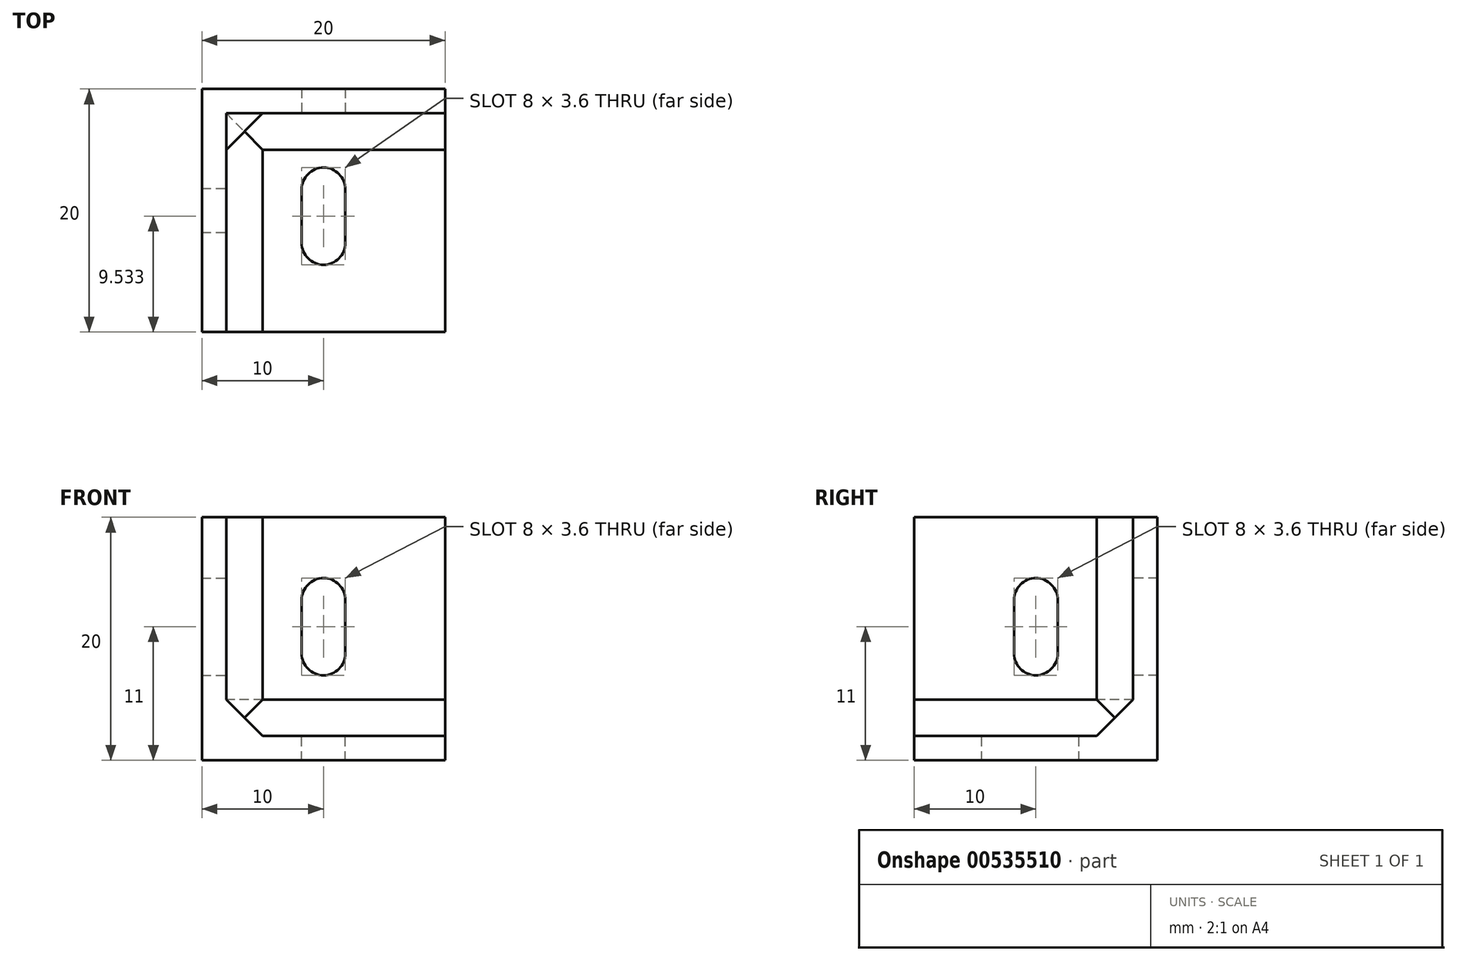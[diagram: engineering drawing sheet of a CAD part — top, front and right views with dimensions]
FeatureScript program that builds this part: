
annotation { "Feature Type Name" : "Feature", "Feature Type Description" : "" }
export const myFeature = defineFeature(function(context is Context, id is Id, definition is map)
    precondition{}
    {
        {
            var Q0;
            Q0=qCreatedBy(makeId("Top.planeOp"),FACE);
            var sketch = newSketch(context, id + "F0", { "sketchPlane" : qUnion([Q0])});
            skLineSegment(sketch, "E0.bottom", {"start": v(10, -10) * mm, "end": v(-10, -10) * mm});
            skLineSegment(sketch, "E0.top", {"start": v(10, 10) * mm, "end": v(-10, 10) * mm});
            skLineSegment(sketch, "E0.left", {"start": v(10, -10) * mm, "end": v(10, 10) * mm});
            skLineSegment(sketch, "E0.right", {"start": v(-10, -10) * mm, "end": v(-10, 10) * mm});
            skPoint(sketch, "E0.middle", {"position": v(0, 0) * mm});
            skSolve(sketch);
        }
        {
            var Q0;
            Q0=makeQuery(id+"F0.imprint","IMPRINT",FACE,{"disambiguationData":[TD([[makeQuery(id+"F0.imprint","IMPRINT",EDGE,{"derivedFrom":sQuery(id+"F0.wireOp",EDGE,"E0.bottom")}),-1.0]])]});
            extrude(context, id + "F1", {"entities" : qUnion([Q0]), "depth" : 2 * mm, "offsetDistance" : 25 * mm});
        }
        {
            var Q0;
            Q0=makeQuery(id+"F1.opExtrude","CAP_FACE",FACE,{"disambiguationData":[OSD([sQuery(id+"F0.wireOp",EDGE,"E0.bottom"),sQuery(id+"F0.wireOp",EDGE,"E0.top"),sQuery(id+"F0.wireOp",EDGE,"E0.left"),sQuery(id+"F0.wireOp",EDGE,"E0.right")])],"isStart":false});
            var sketch = newSketch(context, id + "F2", { "sketchPlane" : qUnion([Q0])});
            skLineSegment(sketch, "E1", {"start": v(-8, -10) * mm, "end": v(-10, -10) * mm});
            skLineSegment(sketch, "E2", {"start": v(-10, -10) * mm, "end": v(-10, 10) * mm});
            skLineSegment(sketch, "E3", {"start": v(-10, 10) * mm, "end": v(10, 10) * mm});
            skLineSegment(sketch, "E4", {"start": v(10, 10) * mm, "end": v(10, 8) * mm});
            skLineSegment(sketch, "E5", {"start": v(10, 8) * mm, "end": v(-8, 8) * mm});
            skLineSegment(sketch, "E6", {"start": v(-8, 8) * mm, "end": v(-8, -10) * mm});
            skSolve(sketch);
        }
        {
            var Q0;
            Q0=makeQuery(id+"F2.imprint","IMPRINT",FACE,{"disambiguationData":[TD([[makeQuery(id+"F2.imprint","IMPRINT",EDGE,{"derivedFrom":sQuery(id+"F2.wireOp",EDGE,"E1")}),-1.0]])]});
            extrude(context, id + "F3", {"entities" : qUnion([Q0]), "operationType" : NewBodyOperationType.ADD, "depth" : 18 * mm, "offsetDistance" : 25 * mm});
        }
        {
            var Q0;
            Q0=makeQuery(id+"F1.opExtrude","CAP_FACE",FACE,{"disambiguationData":[OSD([sQuery(id+"F0.wireOp",EDGE,"E0.bottom"),sQuery(id+"F0.wireOp",EDGE,"E0.top"),sQuery(id+"F0.wireOp",EDGE,"E0.left"),sQuery(id+"F0.wireOp",EDGE,"E0.right")])],"isStart":false});
            var sketch = newSketch(context, id + "F4", { "sketchPlane" : qUnion([Q0])});
            skLineSegment(sketch, "E7.bottom", {"start": v(0, -4.47) * mm, "end": v(0, -4.47) * mm});
            skLineSegment(sketch, "E7.top", {"start": v(0, 3.53) * mm, "end": v(0, 3.53) * mm});
            skLineSegment(sketch, "E7.left", {"start": v(1.8, -2.67) * mm, "end": v(1.8, 1.73) * mm});
            skLineSegment(sketch, "E7.right", {"start": v(-1.8, -2.67) * mm, "end": v(-1.8, 1.73) * mm});
            skPoint(sketch, "E7.middle", {"position": v(0, -0.47) * mm});
            skPoint(sketch, "E8.visualSharp", {"position": v(-1.8, 3.53) * mm});
            skArc(sketch, "E8.filletArc", {"start": v(0, 3.53) * mm, "mid": v(-1.27, 3) * mm, "end": v(-1.8, 1.73) * mm});
            skPoint(sketch, "E9.visualSharp", {"position": v(1.8, 3.53) * mm});
            skArc(sketch, "E9.filletArc", {"start": v(1.8, 1.73) * mm, "mid": v(1.27, 3) * mm, "end": v(0, 3.53) * mm});
            skPoint(sketch, "E10.visualSharp", {"position": v(-1.8, -4.47) * mm});
            skArc(sketch, "E10.filletArc", {"start": v(-1.8, -2.67) * mm, "mid": v(-1.27, -3.94) * mm, "end": v(0, -4.47) * mm});
            skPoint(sketch, "E11.visualSharp", {"position": v(1.8, -4.47) * mm});
            skArc(sketch, "E11.filletArc", {"start": v(0, -4.47) * mm, "mid": v(1.27, -3.94) * mm, "end": v(1.8, -2.67) * mm});
            skSolve(sketch);
        }
        {
            var Q0;
            Q0=makeQuery(id+"F3.opExtrude","SWEPT_FACE",FACE,{"disambiguationData":[OSD([sQuery(id+"F2.wireOp",EDGE,"E6")])]});
            var sketch = newSketch(context, id + "F5", { "sketchPlane" : qUnion([Q0])});
            skLineSegment(sketch, "E12.bottom", {"start": v(0, 7) * mm, "end": v(0, 7) * mm});
            skLineSegment(sketch, "E12.top", {"start": v(0, 15) * mm, "end": v(0, 15) * mm});
            skLineSegment(sketch, "E12.left", {"start": v(1.8, 8.8) * mm, "end": v(1.8, 13.2) * mm});
            skLineSegment(sketch, "E12.right", {"start": v(-1.8, 8.8) * mm, "end": v(-1.8, 13.2) * mm});
            skPoint(sketch, "E12.middle", {"position": v(0, 11) * mm});
            skPoint(sketch, "E13.visualSharp", {"position": v(-1.8, 15) * mm});
            skArc(sketch, "E13.filletArc", {"start": v(0, 15) * mm, "mid": v(-1.27, 14.47) * mm, "end": v(-1.8, 13.2) * mm});
            skPoint(sketch, "E14.visualSharp", {"position": v(1.8, 7) * mm});
            skArc(sketch, "E14.filletArc", {"start": v(0, 7) * mm, "mid": v(1.27, 7.53) * mm, "end": v(1.8, 8.8) * mm});
            skPoint(sketch, "E15.visualSharp", {"position": v(1.8, 15) * mm});
            skArc(sketch, "E15.filletArc", {"start": v(1.8, 13.2) * mm, "mid": v(1.27, 14.47) * mm, "end": v(0, 15) * mm});
            skPoint(sketch, "E16.visualSharp", {"position": v(-1.8, 7) * mm});
            skArc(sketch, "E16.filletArc", {"start": v(-1.8, 8.8) * mm, "mid": v(-1.27, 7.53) * mm, "end": v(0, 7) * mm});
            skSolve(sketch);
        }
        {
            var Q0;
            Q0=makeQuery(id+"F3.opExtrude","SWEPT_FACE",FACE,{"disambiguationData":[OSD([sQuery(id+"F2.wireOp",EDGE,"E5")])]});
            var sketch = newSketch(context, id + "F6", { "sketchPlane" : qUnion([Q0])});
            skLineSegment(sketch, "E17.bottom", {"start": v(0, 7) * mm, "end": v(0, 7) * mm});
            skLineSegment(sketch, "E17.top", {"start": v(0, 15) * mm, "end": v(0, 15) * mm});
            skLineSegment(sketch, "E17.left", {"start": v(1.8, 8.8) * mm, "end": v(1.8, 13.2) * mm});
            skLineSegment(sketch, "E17.right", {"start": v(-1.8, 8.8) * mm, "end": v(-1.8, 13.2) * mm});
            skPoint(sketch, "E17.middle", {"position": v(0, 11) * mm});
            skPoint(sketch, "E18.visualSharp", {"position": v(-1.8, 15) * mm});
            skArc(sketch, "E18.filletArc", {"start": v(0, 15) * mm, "mid": v(-1.27, 14.47) * mm, "end": v(-1.8, 13.2) * mm});
            skPoint(sketch, "E19.visualSharp", {"position": v(-1.8, 7) * mm});
            skArc(sketch, "E19.filletArc", {"start": v(-1.8, 8.8) * mm, "mid": v(-1.27, 7.53) * mm, "end": v(0, 7) * mm});
            skPoint(sketch, "E20.visualSharp", {"position": v(1.8, 7) * mm});
            skArc(sketch, "E20.filletArc", {"start": v(0, 7) * mm, "mid": v(1.27, 7.53) * mm, "end": v(1.8, 8.8) * mm});
            skPoint(sketch, "E21.visualSharp", {"position": v(1.8, 15) * mm});
            skArc(sketch, "E21.filletArc", {"start": v(1.8, 13.2) * mm, "mid": v(1.27, 14.47) * mm, "end": v(0, 15) * mm});
            skSolve(sketch);
        }
        {
            var Q0;
            Q0=makeQuery(id+"F5.imprint","IMPRINT",FACE,{"disambiguationData":[TD([[makeQuery(id+"F5.imprint","IMPRINT",EDGE,{"derivedFrom":sQuery(id+"F5.wireOp",EDGE,"E12.left")}),1.0]])]});
            extrude(context, id + "F7", {"entities" : qUnion([Q0]), "operationType" : NewBodyOperationType.REMOVE, "endBound" : BoundingType.THROUGH_ALL, "oppositeDirection" : true, "depth" : 25 * mm, "offsetDistance" : 25 * mm});
        }
        {
            var Q0;
            Q0=makeQuery(id+"F6.imprint","IMPRINT",FACE,{"disambiguationData":[TD([[makeQuery(id+"F6.imprint","IMPRINT",EDGE,{"derivedFrom":sQuery(id+"F6.wireOp",EDGE,"E17.left")}),1.0]])]});
            extrude(context, id + "F8", {"entities" : qUnion([Q0]), "operationType" : NewBodyOperationType.REMOVE, "endBound" : BoundingType.THROUGH_ALL, "oppositeDirection" : true, "depth" : 25 * mm, "offsetDistance" : 25 * mm});
        }
        {
            var Q0;
            Q0=makeQuery(id+"F4.imprint","IMPRINT",FACE,{"disambiguationData":[TD([[makeQuery(id+"F4.imprint","IMPRINT",EDGE,{"derivedFrom":sQuery(id+"F4.wireOp",EDGE,"E7.left")}),1.0]])]});
            extrude(context, id + "F9", {"entities" : qUnion([Q0]), "operationType" : NewBodyOperationType.REMOVE, "endBound" : BoundingType.THROUGH_ALL, "oppositeDirection" : true, "depth" : 25 * mm, "offsetDistance" : 25 * mm});
        }
        {
            var Q0;
            Q0=makeQuery(id+"F3.boolean.opBoolean","MERGE",FACE,{"derivedFrom":[makeQuery(id+"F1.opExtrude","SWEPT_FACE",FACE,{"disambiguationData":[OSD([sQuery(id+"F0.wireOp",EDGE,"E0.left")])]}),makeQuery(id+"F3.opExtrude","SWEPT_FACE",FACE,{"disambiguationData":[OSD([sQuery(id+"F2.wireOp",EDGE,"E4")])]})]});
            var sketch = newSketch(context, id + "F10", { "sketchPlane" : qUnion([Q0])});
            skLineSegment(sketch, "E22", {"start": v(8, 2) * mm, "end": v(5, 2) * mm});
            skLineSegment(sketch, "E23", {"start": v(5, 2) * mm, "end": v(8, 5) * mm});
            skLineSegment(sketch, "E24", {"start": v(8, 5) * mm, "end": v(8, 2) * mm});
            skSolve(sketch);
        }
        {
            var Q0;
            Q0=makeQuery(id+"F10.imprint","IMPRINT",FACE,{"disambiguationData":[TD([[makeQuery(id+"F10.imprint","IMPRINT",EDGE,{"derivedFrom":sQuery(id+"F10.wireOp",EDGE,"E22")}),1.0]])]});
            extrude(context, id + "F11", {"entities" : qUnion([Q0]), "operationType" : NewBodyOperationType.ADD, "endBound" : BoundingType.UP_TO_NEXT, "oppositeDirection" : true, "depth" : 25 * mm, "offsetDistance" : 25 * mm});
        }
        {
            var Q0;
            Q0=makeQuery(id+"F3.boolean.opBoolean","MERGE",FACE,{"derivedFrom":[makeQuery(id+"F1.opExtrude","SWEPT_FACE",FACE,{"disambiguationData":[OSD([sQuery(id+"F0.wireOp",EDGE,"E0.bottom")])]}),makeQuery(id+"F3.opExtrude","SWEPT_FACE",FACE,{"disambiguationData":[OSD([sQuery(id+"F2.wireOp",EDGE,"E1")])]})]});
            var sketch = newSketch(context, id + "F12", { "sketchPlane" : qUnion([Q0])});
            skLineSegment(sketch, "E25", {"start": v(-8, 2) * mm, "end": v(-8, 5) * mm});
            skLineSegment(sketch, "E26", {"start": v(-8, 5) * mm, "end": v(-5, 2) * mm});
            skLineSegment(sketch, "E27", {"start": v(-5, 2) * mm, "end": v(-8, 2) * mm});
            skSolve(sketch);
        }
        {
            var Q0;
            Q0=makeQuery(id+"F12.imprint","IMPRINT",FACE,{"disambiguationData":[TD([[makeQuery(id+"F12.imprint","IMPRINT",EDGE,{"derivedFrom":sQuery(id+"F12.wireOp",EDGE,"E25")}),1.0]])]});
            extrude(context, id + "F13", {"entities" : qUnion([Q0]), "operationType" : NewBodyOperationType.ADD, "endBound" : BoundingType.UP_TO_NEXT, "oppositeDirection" : true, "depth" : 25 * mm, "offsetDistance" : 25 * mm});
        }
        {
            var Q0;
            Q0=makeQuery(id+"F3.opExtrude","CAP_FACE",FACE,{"disambiguationData":[OSD([sQuery(id+"F2.wireOp",EDGE,"E1"),sQuery(id+"F2.wireOp",EDGE,"E2"),sQuery(id+"F2.wireOp",EDGE,"E3"),sQuery(id+"F2.wireOp",EDGE,"E4"),sQuery(id+"F2.wireOp",EDGE,"E5"),sQuery(id+"F2.wireOp",EDGE,"E6")])],"isStart":false});
            var sketch = newSketch(context, id + "F14", { "sketchPlane" : qUnion([Q0])});
            skLineSegment(sketch, "E28", {"start": v(-8, 8) * mm, "end": v(-5, 8) * mm});
            skLineSegment(sketch, "E29", {"start": v(-5, 8) * mm, "end": v(-8, 5) * mm});
            skLineSegment(sketch, "E30", {"start": v(-8, 5) * mm, "end": v(-8, 8) * mm});
            skSolve(sketch);
        }
        {
            var Q0;
            Q0=makeQuery(id+"F14.imprint","IMPRINT",FACE,{"disambiguationData":[TD([[makeQuery(id+"F14.imprint","IMPRINT",EDGE,{"derivedFrom":sQuery(id+"F14.wireOp",EDGE,"E28")}),1.0]])]});
            extrude(context, id + "F15", {"entities" : qUnion([Q0]), "endBound" : BoundingType.UP_TO_NEXT, "oppositeDirection" : true, "depth" : 25 * mm, "offsetDistance" : 25 * mm});
        }
    });
